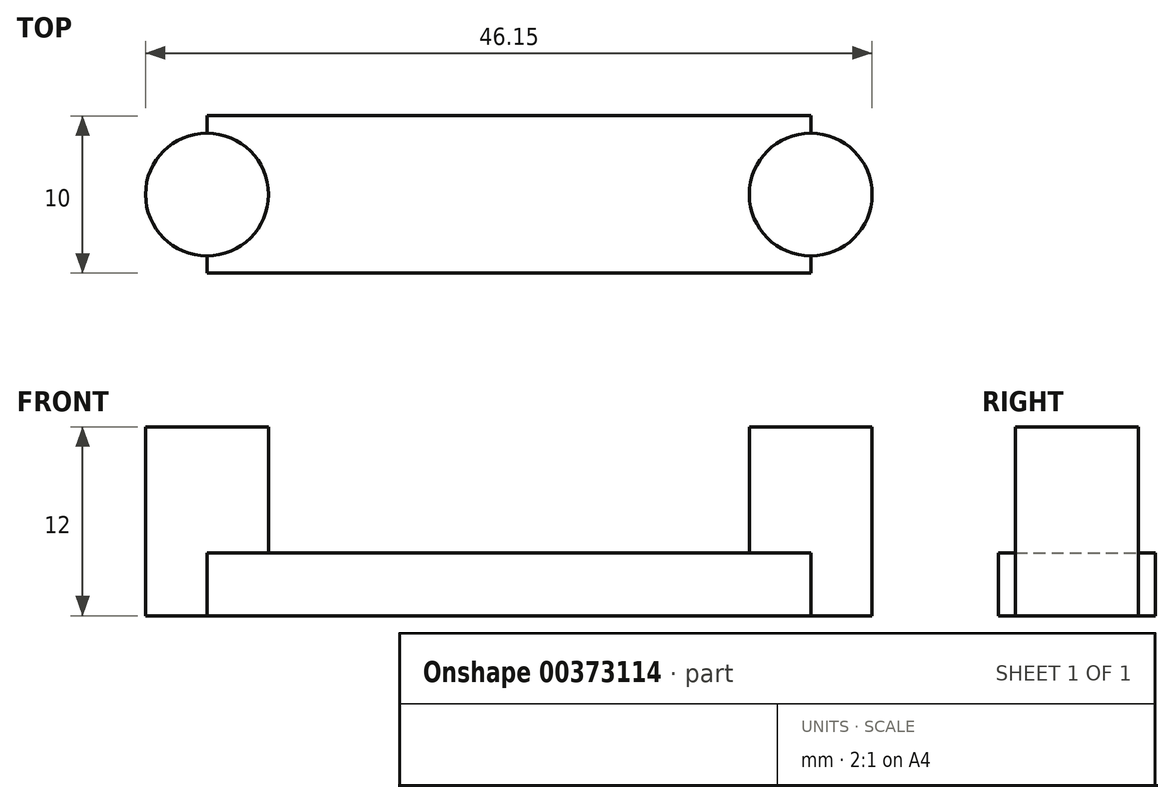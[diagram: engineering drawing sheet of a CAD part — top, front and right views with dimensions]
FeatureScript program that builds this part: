
annotation { "Feature Type Name" : "Feature", "Feature Type Description" : "" }
export const myFeature = defineFeature(function(context is Context, id is Id, definition is map)
    precondition{}
    {
        {
            var Q0;
            Q0=qCreatedBy(makeId("Top.planeOp"),FACE);
            var sketch = newSketch(context, id + "F0", { "sketchPlane" : qUnion([Q0])});
            skLineSegment(sketch, "E0.bottom", {"start": v(-18.1, -0.53) * mm, "end": v(20.25, -0.53) * mm});
            skLineSegment(sketch, "E0.top", {"start": v(-18.1, -10.53) * mm, "end": v(20.25, -10.53) * mm});
            skLineSegment(sketch, "E0.left", {"start": v(-18.1, -0.53) * mm, "end": v(-18.1, -10.53) * mm});
            skLineSegment(sketch, "E0.right", {"start": v(20.25, -0.53) * mm, "end": v(20.25, -10.53) * mm});
            skCircle(sketch, "E1", {"center": v(-18.1, -5.53) * mm, "radius": 3.9 * mm});
            skCircle(sketch, "E2", {"center": v(20.25, -5.53) * mm, "radius": 3.9 * mm});
            skSolve(sketch);
        }
        {
            var Q0;
            {var subQ0=sQuery(id+"F0.wireOp",EDGE,"E1");var subQ1=sQuery(id+"F0.wireOp",EDGE,"E0.left");var subQ2=makeQuery(id+"F0.imprint","INTERSECT",VERTEX,{"disambiguationData":[OD(0.0)],"derivedFrom":[subQ1,subQ0]});Q0=makeQuery(id+"F0.imprint","IMPRINT",FACE,{"disambiguationData":[TD([[makeQuery(id+"F0.imprint","IMPRINT",EDGE,{"disambiguationData":[TD([[subQ2,-1.0]])],"derivedFrom":subQ1}),1.0]])]});}
            var Q1;
            {var subQ0=sQuery(id+"F0.wireOp",EDGE,"E1");var subQ1=sQuery(id+"F0.wireOp",EDGE,"E0.left");var subQ2=makeQuery(id+"F0.imprint","INTERSECT",VERTEX,{"disambiguationData":[OD(0.0)],"derivedFrom":[subQ1,subQ0]});Q1=makeQuery(id+"F0.imprint","IMPRINT",FACE,{"disambiguationData":[TD([[makeQuery(id+"F0.imprint","IMPRINT",EDGE,{"disambiguationData":[TD([[subQ2,-1.0]])],"derivedFrom":subQ1}),-1.0]])]});}
            var Q2;
            {var subQ0=sQuery(id+"F0.wireOp",EDGE,"E2");var subQ1=sQuery(id+"F0.wireOp",EDGE,"E0.right");var subQ2=makeQuery(id+"F0.imprint","INTERSECT",VERTEX,{"disambiguationData":[OD(0.0)],"derivedFrom":[subQ1,subQ0]});Q2=makeQuery(id+"F0.imprint","IMPRINT",FACE,{"disambiguationData":[TD([[makeQuery(id+"F0.imprint","IMPRINT",EDGE,{"disambiguationData":[TD([[subQ2,-1.0]])],"derivedFrom":subQ1}),1.0]])]});}
            var Q3;
            {var subQ0=sQuery(id+"F0.wireOp",EDGE,"E2");var subQ1=sQuery(id+"F0.wireOp",EDGE,"E0.right");var subQ2=makeQuery(id+"F0.imprint","INTERSECT",VERTEX,{"disambiguationData":[OD(0.0)],"derivedFrom":[subQ1,subQ0]});Q3=makeQuery(id+"F0.imprint","IMPRINT",FACE,{"disambiguationData":[TD([[makeQuery(id+"F0.imprint","IMPRINT",EDGE,{"disambiguationData":[TD([[subQ2,-1.0]])],"derivedFrom":subQ1}),-1.0]])]});}
            extrude(context, id + "F1", {"entities" : qUnion([Q0, Q1, Q2, Q3]), "depth" : 12 * mm});
        }
        {
            var Q0;
            {var subQ4=sQuery(id+"F0.wireOp",EDGE,"E0.bottom");Q0=makeQuery(id+"F0.imprint","IMPRINT",FACE,{"disambiguationData":[TD([[makeQuery(id+"F0.imprint","IMPRINT",EDGE,{"derivedFrom":subQ4}),-1.0]])]});}
            extrude(context, id + "F2", {"entities" : qUnion([Q0]), "operationType" : NewBodyOperationType.ADD, "depth" : 4 * mm});
        }
    });
